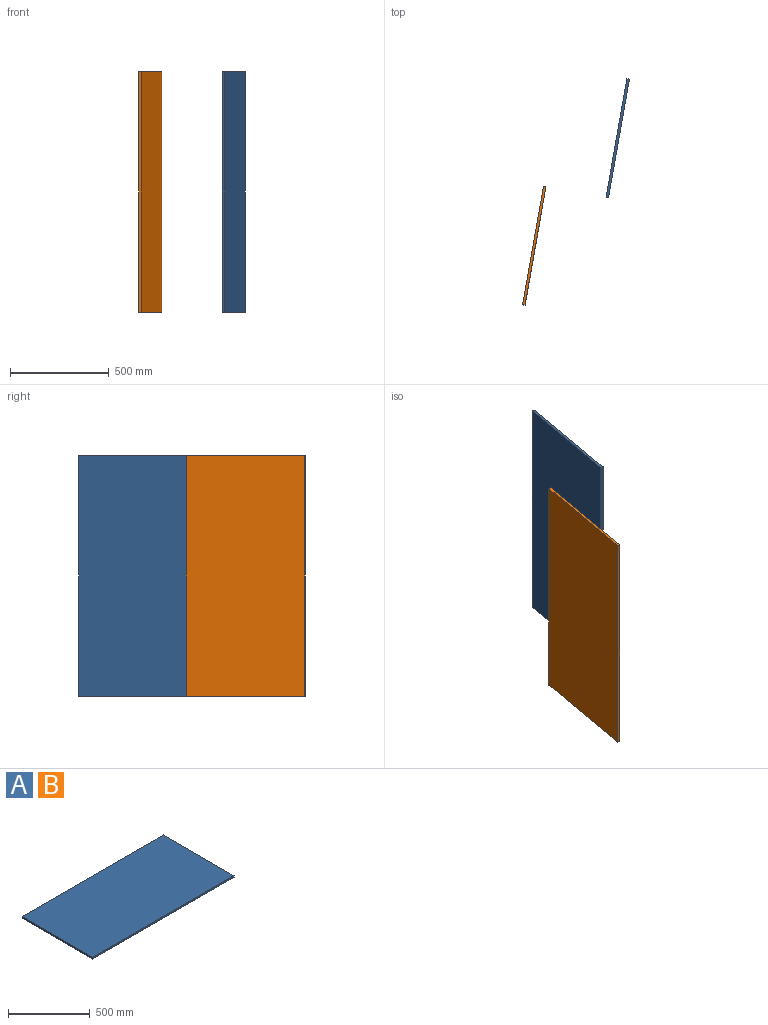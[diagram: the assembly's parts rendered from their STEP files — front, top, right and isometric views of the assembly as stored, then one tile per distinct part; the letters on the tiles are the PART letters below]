
ASSEMBLY  parts=2 mates=1
PART A: 6 faces, bbox 1219.2x609.6x12.7 mm
  f0: plane 609.6x12.7mm, normal (1,0,0), area 7741.9mm2, adj f1,f3,f4,f5
  f1: plane 1219.2x12.7mm, normal (0,1,0), area 15483.8mm2, adj f0,f2,f4,f5
  f2: plane 609.6x12.7mm, normal (-1,0,0), area 7741.9mm2, adj f1,f3,f4,f5
  f3: plane 1219.2x12.7mm, normal (0,-1,0), area 15483.8mm2, adj f0,f2,f4,f5
  f4: plane 1219.2x609.6mm, normal (0,0,1), area 743224.3mm2, adj f0,f1,f2,f3
  f5: plane 1219.2x609.6mm, normal (0,0,-1), area 743224.3mm2, adj f0,f1,f2,f3
PART B: same geometry as A
PLACE A rot(axis=(0.09,0.99,-0.09),90.4deg) t=(36.48,307.9,691.16)mm
PLACE B rot(axis=(0.09,0.99,-0.09),90.4deg) t=(-386.5,-236.52,691.16)mm
MATE slider A.f5 <-> B.f5  axis (-0.98,0.17,0) through (-16.45,7.73,691.16)mm
